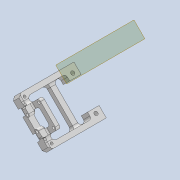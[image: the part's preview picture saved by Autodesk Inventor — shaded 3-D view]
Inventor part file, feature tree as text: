
AUTODESK INVENTOR PART (.ipt)
format: ipt  version: 2020 (Build 240168000, 168)  size: 621,056 bytes
history: native  units: mm
features: projected_geometry x16, sketch x14, thicken_offset x13, extrude x11, fillet x8, other x6, chamfer x5, hole x3, plane x1, reference x1
ambient origin geometry x8: Origin, YZ Plane, XZ Plane, XY Plane, X Axis, Y Axis, Z Axis, Center Point
bodies: Solid1 (feature_tree)
feature tree (78):
  extrude  "Extrusion1"  Depth=4.0mm
  extrude  "Extrusion2"  Depth=4.0mm
  extrude  "Extrusion3"  Depth=2.0mm
  thicken_offset  "Thicken1"
  thicken_offset  "Thicken2"
  thicken_offset  "Thicken3"
  thicken_offset  "Thicken4"
  chamfer  "Chamfer2"  Distance=6.3mm
  fillet  "Fillet5"  Radius=6.0mm
  hole  "Hole1"  [1 undecoded]
  hole  "Hole2"  [1 undecoded]
  plane  "Work Plane1"
  extrude  "Extrusion4"  Depth=0.25mm
  extrude  "Extrusion5"  Depth=0.25mm
  extrude  "Extrusion6"  Depth=1.0mm
  thicken_offset  "Thicken5"
  thicken_offset  "Thicken6"
  thicken_offset  "Thicken7"
  fillet  "Fillet8"  Radius=1.0mm
  chamfer  "Chamfer3"  Distance=1.0mm Angle=45.0deg
  fillet  "Fillet9"  Radius=2.0mm
  fillet  "Fillet10"  Radius=6.0mm
  fillet  "Fillet11"  Radius=6.0mm
  chamfer  "Chamfer4"  Distance=6.0mm
  extrude  "Extrusion7"  Depth=1.0mm
  fillet  "Fillet12"  Radius=35.0mm
  chamfer  "Chamfer5"  Distance=3.5mm
  extrude  "Extrusion8"  Depth=1.0mm
  fillet  "Fillet13"  Radius=3.5mm
  fillet  "Fillet14"  Radius=6.3mm
  extrude  "Extrusion9"  Depth=1.0mm TaperAngle=0.0deg
  extrude  "Extrusion10"  Depth=1.0mm
  extrude  "Extrusion11"  Depth=1.0mm
  sketch  "Sketch14"  dims[d44=1.9mm d45=6.0mm d46=4.0mm d47=2.0mm d48=90.0deg d49=4.0mm d50=0.0mm d51=6.0mm d52=6.0mm d53=6.0mm d54=6.0mm d55=35.0mm d56=3.5mm d57=35.0mm d58=3.5mm d59=6.3mm d60=0.0mm d61=6.3mm d62=0.0mm d63=1.9mm d64=1.9mm d65=6.3mm d66=0.0mm d69=1.5mm d70=1.5mm d71=1.0mm d72=1.5mm d73=1.0mm d74=1.5mm d75=3.0mm d76=1.0mm d77=2.0mm d78=45.0deg d79=1.0mm d80=0.5mm d81=0.5mm d82=2.0mm d83=2.0mm d84=45.0deg d85=5.0mm d86=5.0mm d87=5.0mm d88=5.0mm d89=2.0mm d90=0.0mm d91=3.0mm d92=1.0mm d93=2.0mm d94=45.0deg d95=7.0mm d96=29.0mm d97=4.0mm d98=3.5mm d99=0.0mm d100=2.2mm d104=2.0mm d109=2.0mm d110=2.0mm d111=2.0mm d112=2.0mm d113=8.0mm d114=0.0mm d115=8.0mm d116=10.0mm d117=2.0mm d118=2.0mm d119=8.0mm d120=0.0mm d121=10.0mm d122=0.0mm d123=2.0mm d124=2.0mm d125=2.0mm d126=2.0mm d127=2.0mm d128=3.0mm d129=2.0mm d130=3.0mm d131=1.8mm d132=6.0mm d133=4.0mm d134=2.0mm d135=90.0deg d136=10.0mm d137=0.0mm d138=3.0mm d139=2.0mm d140=45.0deg d141=1.0mm d142=1.0mm d143=1.0mm d144=1.0mm d18=0.5mm d19=0.872665mm]
  thicken_offset  "Thicken10"
  thicken_offset  "Thicken11"
  thicken_offset  "Thicken12"
  thicken_offset  "Thicken13"
  hole  "Hole3"  [1 undecoded]
  chamfer  "Chamfer7"  Distance=1.5mm
  thicken_offset  "Thicken14"
  thicken_offset  "Thicken15"
  sketch  "Sketch1"  dims[d0=4.0mm d1=4.0mm]
  reference  "Reference1"
  sketch  "Sketch2"  dims[d2=4.0mm d3=4.0mm]
  projected_geometry  "Projected Loop1"
  sketch  "Sketch3"  dims[d4=2.0mm d5=0.0mm d6=5.5mm]
  projected_geometry  "Projected Loop2"
  projected_geometry  "Projected Loop3"
  projected_geometry  "Projected Loop4"
  sketch  "Sketch4"  dims[d7=4.0mm]
  projected_geometry  "Projected Loop5"
  projected_geometry  "Projected Loop6"
  sketch  "Sketch5"  dims[d8=4.0mm]
  projected_geometry  "Projected Loop7"
  projected_geometry  "Projected Loop8"
  sketch  "Sketch6"  dims[d9=4.0mm d10=6.3mm d11=0.0mm d12=6.0mm]
  sketch  "Sketch7"  dims[d13=4.0mm d14=6.0mm]
  projected_geometry  "Projected Loop9"
  projected_geometry  "Projected Loop10"
  sketch  "Sketch8"  dims[d15=4.0mm d16=6.0mm d17=0.0mm]
  projected_geometry  "Projected Loop11"
  sketch  "Sketch9"  dims[d21=0.25mm d22=0.25mm]
  projected_geometry  "Projected Loop12"
  sketch  "Sketch10"  dims[d23=0.25mm d24=0.25mm]
  projected_geometry  "Projected Loop13"
  sketch  "Sketch11"  dims[d27=1.0mm d28=1.0mm d29=1.0mm]
  projected_geometry  "Projected Loop14"
  projected_geometry  "Projected Loop15"
  sketch  "Sketch12"  dims[d30=1.0mm d33=1.0mm d34=2.0mm d35=45.0deg d36=2.0mm]
  projected_geometry  "Projected Loop16"
  sketch  "Sketch13"  dims[d37=1.9mm d38=6.0mm d39=4.0mm d40=2.0mm d41=90.0deg d42=4.0mm d43=0.0mm]
  parser-record x2  (decoder bookkeeping rows leaked as tree rows — omitted from the tree; the rows remain in map.json)
  other  "mot_27_ass.iam"
  other  "mot_27_2:1"
  other  "tip_3_ass_base.iam"
  other  "ext_shell_2:1"
note: 3 required parameter values undecoded (feature->parameter linkage not recoverable at this tier; creation-order binding heuristic only, values carry confidence <= 0.55)
note: 2 file-system paths scrubbed to <path> (originals preserved in map.json)
